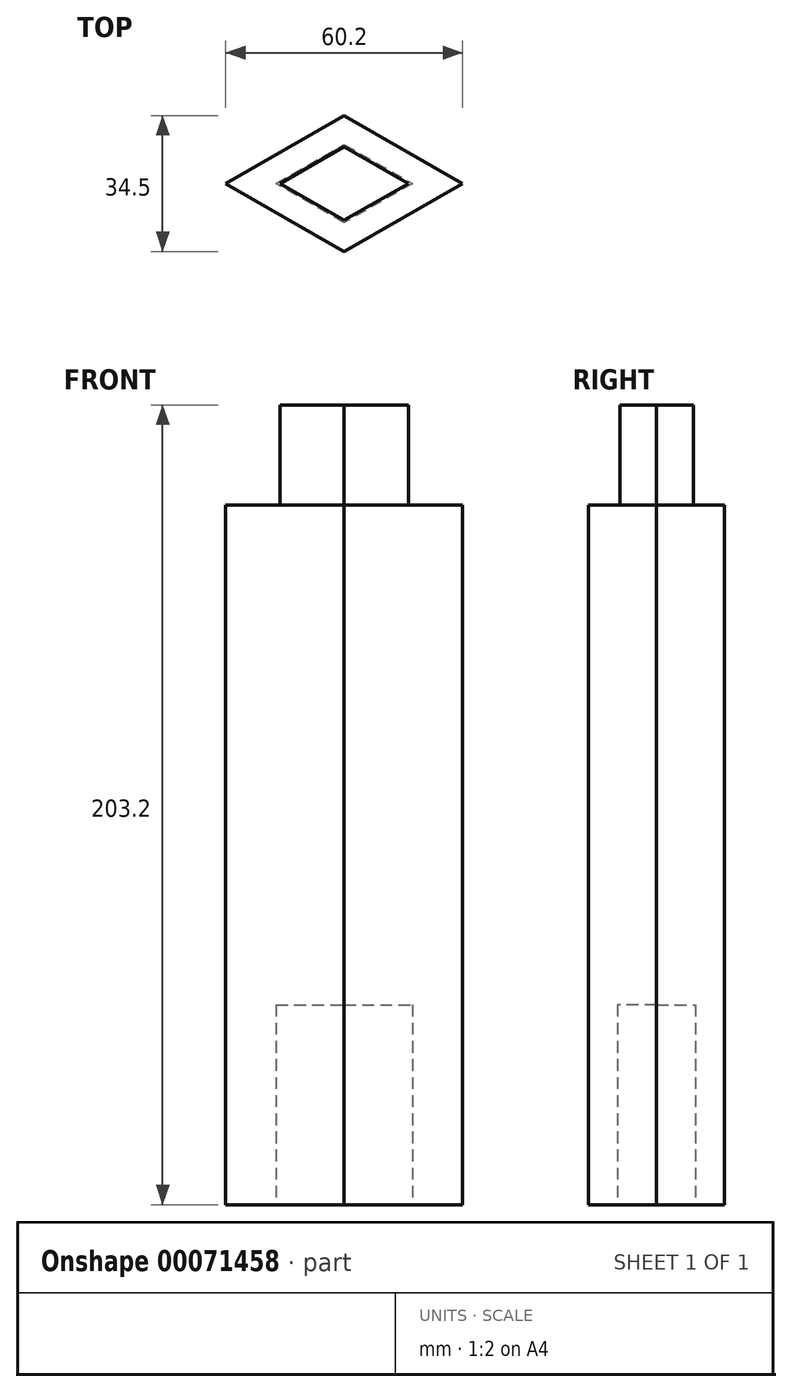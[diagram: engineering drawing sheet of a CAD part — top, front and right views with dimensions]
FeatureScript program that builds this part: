
annotation { "Feature Type Name" : "Feature", "Feature Type Description" : "" }
export const myFeature = defineFeature(function(context is Context, id is Id, definition is map)
    precondition{}
    {
        {
            var Q0;
            Q0=qCreatedBy(makeId("Top.planeOp"),FACE);
            var sketch = newSketch(context, id + "F0", { "sketchPlane" : qUnion([Q0])});
            skLineSegment(sketch, "E0", {"start": v(0, 0) * mm, "end": v(-30.1, 0) * mm});
            skLineSegment(sketch, "E1", {"start": v(0, 0) * mm, "end": v(0, 17.25) * mm});
            skLineSegment(sketch, "E2.MirrorCS", {"start": v(0, 0) * mm, "end": v(30.1, 0) * mm});
            skLineSegment(sketch, "E3.MirrorCS", {"start": v(0, 0) * mm, "end": v(0, -17.25) * mm});
            skLineSegment(sketch, "E4", {"start": v(-30.1, 0) * mm, "end": v(0, 17.25) * mm});
            skLineSegment(sketch, "E5", {"start": v(0, 17.25) * mm, "end": v(30.1, 0) * mm});
            skLineSegment(sketch, "E6", {"start": v(30.1, 0) * mm, "end": v(0, -17.25) * mm});
            skLineSegment(sketch, "E7", {"start": v(0, -17.25) * mm, "end": v(-30.1, 0) * mm});
            skLineSegment(sketch, "E8.0", {"start": v(-17.33, 0) * mm, "end": v(0, 9.93) * mm});
            skLineSegment(sketch, "E8.1", {"start": v(0, -9.93) * mm, "end": v(-17.33, 0) * mm});
            skLineSegment(sketch, "E8.2", {"start": v(17.33, 0) * mm, "end": v(0, -9.93) * mm});
            skLineSegment(sketch, "E8.3", {"start": v(0, 9.93) * mm, "end": v(17.33, 0) * mm});
            skSolve(sketch);
        }
        {
            var Q0;
            {var subQ0=sQuery(id+"F0.wireOp",EDGE,"E4");Q0=makeQuery(id+"F0.imprint","IMPRINT",FACE,{"disambiguationData":[TD([[makeQuery(id+"F0.imprint","IMPRINT",EDGE,{"derivedFrom":subQ0}),-1.0]])]});}
            var Q1;
            {var subQ0=sQuery(id+"F0.wireOp",EDGE,"E5");Q1=makeQuery(id+"F0.imprint","IMPRINT",FACE,{"disambiguationData":[TD([[makeQuery(id+"F0.imprint","IMPRINT",EDGE,{"derivedFrom":subQ0}),-1.0]])]});}
            var Q2;
            {var subQ0=sQuery(id+"F0.wireOp",EDGE,"E6");Q2=makeQuery(id+"F0.imprint","IMPRINT",FACE,{"disambiguationData":[TD([[makeQuery(id+"F0.imprint","IMPRINT",EDGE,{"derivedFrom":subQ0}),-1.0]])]});}
            var Q3;
            {var subQ0=sQuery(id+"F0.wireOp",EDGE,"E7");Q3=makeQuery(id+"F0.imprint","IMPRINT",FACE,{"disambiguationData":[TD([[makeQuery(id+"F0.imprint","IMPRINT",EDGE,{"derivedFrom":subQ0}),-1.0]])]});}
            extrude(context, id + "F1", {"entities" : qUnion([Q0, Q1, Q2, Q3]), "depth" : 50.8 * mm});
        }
        {
            var Q0;
            Q0=makeQuery(id+"F1.opExtrude","CAP_FACE",FACE,{"disambiguationData":[OSD([sQuery(id+"F0.wireOp",EDGE,"E4"),sQuery(id+"F0.wireOp",EDGE,"E5"),sQuery(id+"F0.wireOp",EDGE,"E6"),sQuery(id+"F0.wireOp",EDGE,"E7"),sQuery(id+"F0.wireOp",EDGE,"E8.0"),sQuery(id+"F0.wireOp",EDGE,"E8.1"),sQuery(id+"F0.wireOp",EDGE,"E8.2"),sQuery(id+"F0.wireOp",EDGE,"E8.3")])],"isStart":false});
            var sketch = newSketch(context, id + "F2", { "sketchPlane" : qUnion([Q0])});
            skSolve(sketch);
        }
        {
            var Q0;
            Q0=makeQuery(id+"F2.imprint","IMPRINT",FACE,{"disambiguationData":[TD([[makeQuery(id+"F2.imprint","IMPRINT",EDGE,{"derivedFrom":makeQuery(id+"F1.opExtrude","CAP_EDGE",EDGE,{"disambiguationData":[OSD([sQuery(id+"F0.wireOp",EDGE,"E8.0")])],"isStart":false})}),-1.0]])]});
            var Q1;
            Q1=makeQuery(id+"F2.imprint","IMPRINT",FACE,{"disambiguationData":[TD([[makeQuery(id+"F2.imprint","IMPRINT",EDGE,{"derivedFrom":makeQuery(id+"F1.opExtrude","CAP_EDGE",EDGE,{"disambiguationData":[OSD([sQuery(id+"F0.wireOp",EDGE,"E4")])],"isStart":false})}),-1.0]])]});
            extrude(context, id + "F3", {"entities" : qUnion([Q0, Q1]), "operationType" : NewBodyOperationType.ADD, "depth" : 127 * mm});
        }
        {
            var Q0;
            Q0=makeQuery(id+"F3.opExtrude","CAP_FACE",FACE,{"disambiguationData":[OSD([sQuery(id+"F0.wireOp",EDGE,"E4"),sQuery(id+"F0.wireOp",EDGE,"E5"),sQuery(id+"F0.wireOp",EDGE,"E6"),sQuery(id+"F0.wireOp",EDGE,"E7")])],"isStart":false});
            var sketch = newSketch(context, id + "F4", { "sketchPlane" : qUnion([Q0])});
            skLineSegment(sketch, "E9.0", {"start": v(-16.3, 0) * mm, "end": v(0, 9.34) * mm});
            skLineSegment(sketch, "E9.1", {"start": v(0, -9.34) * mm, "end": v(-16.3, 0) * mm});
            skLineSegment(sketch, "E9.2", {"start": v(16.3, 0) * mm, "end": v(0, -9.34) * mm});
            skLineSegment(sketch, "E9.3", {"start": v(0, 9.34) * mm, "end": v(16.3, 0) * mm});
            skSolve(sketch);
        }
        {
            var Q0;
            Q0=makeQuery(id+"F4.imprint","IMPRINT",FACE,{"disambiguationData":[TD([[makeQuery(id+"F4.imprint","IMPRINT",EDGE,{"derivedFrom":sQuery(id+"F4.wireOp",EDGE,"E9.0")}),-1.0]])]});
            extrude(context, id + "F5", {"entities" : qUnion([Q0]), "operationType" : NewBodyOperationType.ADD, "depth" : 25.4 * mm});
        }
    });
